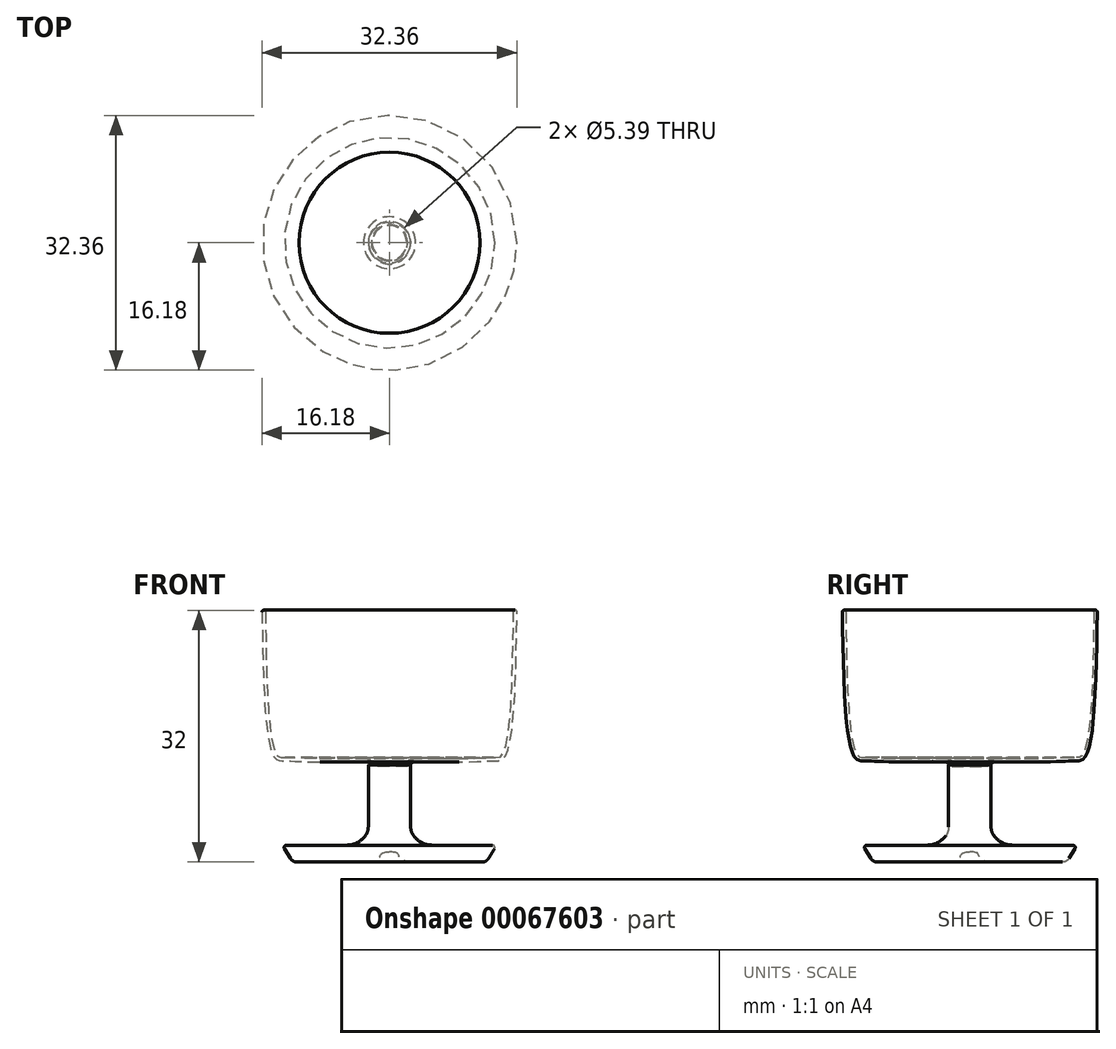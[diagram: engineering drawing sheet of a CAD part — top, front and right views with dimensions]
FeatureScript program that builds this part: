
annotation { "Feature Type Name" : "Feature", "Feature Type Description" : "" }
export const myFeature = defineFeature(function(context is Context, id is Id, definition is map)
    precondition{}
    {
        {
            var Q0;
            Q0=qCreatedBy(makeId("Front.planeOp"),FACE);
            var sketch = newSketch(context, id + "F0", { "sketchPlane" : qUnion([Q0])});
            skLineSegment(sketch, "E0", {"start": v(3.3, 0) * mm, "end": v(11.74, 0) * mm});
            skLineSegment(sketch, "E1", {"start": v(12.58, 0.47) * mm, "end": v(13.34, 1.69) * mm});
            skLineSegment(sketch, "E2", {"start": v(13.08, 2.16) * mm, "end": v(5.4, 2.16) * mm});
            skLineSegment(sketch, "E3", {"start": v(3.11, 3.3) * mm, "end": v(3.06, 3.37) * mm});
            skLineSegment(sketch, "E4", {"start": v(2.7, 4.46) * mm, "end": v(2.7, 12.33) * mm});
            skFitSpline(sketch, "E5", {"points": [v(2.7, 12.33) * mm, v(2.7, 12.59) * mm, v(8.72, 12.72) * mm, v(13.18, 12.86) * mm, v(14.62, 13.32) * mm, v(16.18, 31.79) * mm], "startDerivative": vector(-2.63, 6.06) * mm, "endDerivative": vector(0.97, 62) * mm});
            skFitSpline(sketch, "E6.0", {"points": [v(2.3, 12.16) * mm, v(2.3, 12.18) * mm, v(2.28, 12.21) * mm, v(2.25, 12.3) * mm, v(2.22, 12.4) * mm, v(2.21, 12.57) * mm, v(2.27, 12.76) * mm, v(2.4, 12.91) * mm, v(2.54, 13) * mm, v(2.66, 13.05) * mm, v(2.78, 13.09) * mm, v(2.95, 13.12) * mm, v(3.19, 13.16) * mm, v(3.51, 13.18) * mm, v(3.89, 13.2) * mm, v(4.3, 13.21) * mm, v(4.9, 13.21) * mm, v(5.71, 13.2) * mm, v(6.76, 13.18) * mm, v(7.8, 13.16) * mm, v(8.8, 13.15) * mm, v(9.7, 13.16) * mm, v(10.51, 13.18) * mm, v(11.25, 13.21) * mm, v(11.9, 13.24) * mm, v(12.5, 13.27) * mm, v(12.94, 13.29) * mm, v(13.28, 13.29) * mm, v(13.58, 13.29) * mm, v(13.8, 13.3) * mm, v(13.98, 13.35) * mm, v(14.07, 13.4) * mm, v(14.17, 13.46) * mm, v(14.27, 13.57) * mm, v(14.38, 13.74) * mm, v(14.54, 14.07) * mm, v(14.73, 14.64) * mm, v(14.93, 15.54) * mm, v(15.1, 16.63) * mm, v(15.3, 18.32) * mm, v(15.47, 20.8) * mm, v(15.6, 24.2) * mm, v(15.7, 27.92) * mm, v(15.73, 30.5) * mm, v(15.75, 31.8) * mm]});
            skArc(sketch, "E7", {"start": v(16.18, 31.79) * mm, "mid": v(15.97, 32) * mm, "end": v(15.75, 31.8) * mm});
            skPoint(sketch, "E8.end.orphan", {"position": v(3.14, 12.59) * mm});
            skLineSegment(sketch, "E9", {"start": v(11.5, 13.22) * mm, "end": v(0, 13.22) * mm});
            skPoint(sketch, "E10.visualSharp", {"position": v(2.7, 3.86) * mm});
            skArc(sketch, "E10.filletArc", {"start": v(2.7, 4.46) * mm, "mid": v(2.79, 3.89) * mm, "end": v(3.06, 3.37) * mm});
            skPoint(sketch, "E11.visualSharp", {"position": v(3.97, 2.16) * mm});
            skArc(sketch, "E11.filletArc", {"start": v(3.11, 3.3) * mm, "mid": v(4.12, 2.46) * mm, "end": v(5.4, 2.16) * mm});
            skPoint(sketch, "E12.visualSharp", {"position": v(13.63, 2.16) * mm});
            skArc(sketch, "E12.filletArc", {"start": v(13.34, 1.69) * mm, "mid": v(13.35, 2) * mm, "end": v(13.08, 2.16) * mm});
            skFitSpline(sketch, "E13", {"points": [v(3.3, 0) * mm, v(1.4, 0.39) * mm, v(1.01, 1.09) * mm, v(0, 1.28) * mm], "startDerivative": vector(-5.63, 0.24) * mm, "endDerivative": vector(-3.98, 0) * mm});
            skPoint(sketch, "E14.visualSharp", {"position": v(12.29, 0) * mm});
            skArc(sketch, "E14.filletArc", {"start": v(11.74, 0) * mm, "mid": v(12.22, 0.12) * mm, "end": v(12.58, 0.47) * mm});
            skSolve(sketch);
        }
        {
            var Q0;
            Q0=qCreatedBy(makeId("Right.planeOp"),FACE);
            var sketch = newSketch(context, id + "F1", { "sketchPlane" : qUnion([Q0])});
            skLineSegment(sketch, "E15", {"start": v(0, 0) * mm, "end": v(0, 30.88) * mm});
            skSolve(sketch);
        }
        {
            var Q0;
            Q0 = qSketchRegion(id + "F0", true);
            var Q1;
            Q1 = qConstructionFilter(qBodyType(qCreatedBy(id + "F0" ,EDGE), BodyType.WIRE), ConstructionObject.NO);
            var Q2;
            Q2=sQuery(id+"F1.wireOp",EDGE,"E15");
            revolve(context, id + "F2", {"bodyType" : ToolBodyType.SURFACE, "entities" : qUnion([Q0]), "surfaceEntities" : qUnion([Q1]), "axis" : qUnion([Q2]), "revolveType" : RevolveType.FULL});
        }
    });
